# Revit family: НЕВАТОМ_Решетка защитная VO круглая, версия 1
name_source: partatom
category: Арматура воздуховодов
revit_build: Autodesk Revit 2017 (Build: 20170118_1100(x64)
units: mm (PartAtom-declared; Revit-internal decimal feet)

## family parameters
Всегда вертикально = Да
На основе рабочей плоскости = Нет
Общий = Нет
При загрузке вырезать с полостями = Нет
Размер круглого соединителя = Использовать диаметр
Тип детали = Вставляется

## types (11) — shared parameters
ADSK_Единица измерения = шт.
ADSK_Завод-изготовитель = NEVATOM
Nevatom_URL = https://t.me
длина = 1784 мм
материал = Сталь оцинкованная
ширина = 1784 мм
ширина ободка = 5 мм
ширина решетки = 5 мм

## per-type parameters (varying)
| type | ADSK_Марка | ADSK_Наименование | D | d |
| Решетка защитная VO №4,0  D500 | VO №4,0  D500 | Решетка защитная VO №4,0  D500 | 500 мм | 450 мм |
| Решетка защитная VO №4,5  D560 | VO №4,5  D560 | Решетка защитная VO №4,5  D560 | 560 мм | 510 мм |
| Решетка защитная VO №5,0  D630 | VO №5,0  D630 | Решетка защитная VO №5,0  D630 | 630 мм | 580 мм |
| Решетка защитная VO №5,6  D710 | VO №5,6  D710 | Решетка защитная VO №5,6  D710 | 710 мм | 660 мм |
| Решетка защитная VO №7,1  D900 | VO №7,1  D900 | Решетка защитная VO №7,1  D900 | 900 мм | 850 мм |
| Решетка защитная VO №8,0 D1000 | VO №8,0 D1000 | Решетка защитная VO №8,0 D1000 | 1000 мм | 950 мм |
| Решетка защитная VO №9,0 D1120 | VO №9,0 D1120 | Решетка защитная VO №9,0 D1120 | 1120 мм | 1070 мм |
| Решетка защитная VO №10,0  D1250 | VO №10 D1250 | Решетка защитная VO №10 D1250 | 1250 мм | 1200 мм |
| Решетка защитная VO №12,5 D1600 | VO №12,5 D1600 | Решетка защитная VO №12,5 D1600 | 1600 мм | 1550 мм |
| Решетка защитная VO №6,3  D800 | VO №6,3  D800 | Решетка защитная VO №6,3  D800 | 800 мм | 750 мм |
| Решетка защитная VO №11,2 D1400 | VO №11,2 D1400 | Решетка защитная VO №11,2 D1400 | 1400 мм | 1350 мм |
